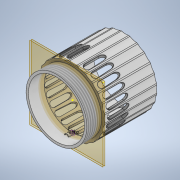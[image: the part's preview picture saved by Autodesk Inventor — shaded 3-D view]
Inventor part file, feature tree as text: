
AUTODESK INVENTOR PART (.ipt)
format: ipt  version: 2020.2 (Build 242310000, 310)  size: 3,711,488 bytes
history: native  units: mm
features: sketch x20, extrude x16, plane x16, thread x4, chamfer x3, mirror x3, pattern_circular x2, emboss x1, revolve x1, split x1, projected_geometry x1
ambient origin geometry x8: Origin, YZ Plane, XZ Plane, XY Plane, X Axis, Y Axis, Z Axis, Center Point
bodies: Solid1 (feature_tree), Solid2 (feature_tree), Solid3 (feature_tree)
feature tree (68):
  extrude  "Extrusion1"  Depth=2.0mm
  plane  "Work Plane1"
  sketch  "Sketch2"  dims[d2=4.714404mm d3=0.428883mm d4=250.0mm d6=360.0deg d8=45.0mm d9=0.0mm d11=10.0mm d12=0.0mm]
  extrude  "Extrusion2"  Depth=10.0mm
  chamfer  "Chamfer1"  Distance=250.0mm Angle=360.0deg
  chamfer  "Chamfer2"  Distance=45.0mm
  chamfer  "Chamfer3"  Distance=10.0mm
  extrude  "Extrusion3"  Depth=10.0mm TaperAngle=360.0deg
  pattern_circular  "Circular Pattern1"  Count=4 Angle=360.0deg
  sketch  "Sketch5"  dims[d18=0.9mm d19=2.0mm d20=45.0deg]
  extrude  "Extrusion4"  Depth=10.0mm TaperAngle=0.0deg
  extrude  "Extrusion5"  Depth=9.1mm TaperAngle=0.0deg
  plane  "Work Plane3"
  plane  "Work Plane4"
  extrude  "Extrusion6"  Depth=2.5mm
  plane  "Work Plane7"
  plane  "Work Plane8"
  sketch  "Sketch7"  dims[d24=0.2mm d25=2.0mm d26=45.0deg]
  plane  "Work Plane9"
  emboss  "Emboss1"
  sketch  "Sketch10"  dims[d29=20.022194mm]
  revolve  "Revolution1"  [1 undecoded]
  pattern_circular  "Circular Pattern2"  Count=3  [1 undecoded]
  extrude  "Extrusion7"  Depth=0.02mm
  sketch  "Sketch13"  dims[d32=35.0mm d33=0.0mm]
  extrude  "Extrusion8"  Depth=2.5mm
  mirror  "Mirror1"
  thread  "Thread1"  [1 undecoded]
  thread  "Thread2"  [1 undecoded]
  extrude  "Extrusion9"  [1 undecoded]
  extrude  "Extrusion10"  Depth=0.5mm TaperAngle=0.0deg
  thread  "Thread3"  [1 undecoded]
  plane  "Work Plane10"
  plane  "Work Plane11"
  split  "Split1"
  extrude  "Extrusion11"  Depth=2.5mm
  thread  "Thread4"  [1 undecoded]
  plane  "Work Plane12"
  plane  "Work Plane14"
  extrude  "Extrusion12"  Depth=4.0mm TaperAngle=0.0deg
  plane  "Work Plane15"
  mirror  "Mirror2"
  sketch  "Sketch21"  dims[d47=10.0mm d48=0.0mm d49=9.1mm d50=0.0mm]
  extrude  "Extrusion13"  [1 undecoded]
  plane  "Work Plane16"
  sketch  "Sketch22"  dims[d51=9.1mm d52=0.0mm d53=9.1mm d54=0.0mm]
  plane  "Work Plane17"
  extrude  "Extrusion14"  Depth=2.5mm TaperAngle=0.0deg
  extrude  "Extrusion15"  Depth=2.5mm TaperAngle=0.0deg
  extrude  "Extrusion16"  Depth=2.5mm TaperAngle=0.0deg
  mirror  "Mirror3"
  sketch  "Sketch1"  dims[d0=45.0mm d1=2.0mm]
  sketch  "Sketch4"  dims[d13=10.0mm d14=0.0mm d15=250.0mm d16=360.0deg]
  sketch  "Sketch6"  dims[d21=0.9mm d22=2.0mm d23=45.0deg]
  plane  "Work Plane5"
  plane  "Work Plane6"
  sketch  "Sketch9"  dims[d27=10.0mm d28=0.0mm]
  sketch  "Sketch11"  dims[d30=1.170635mm]
  sketch  "Sketch12"  dims[d31=2.0mm]
  sketch  "Sketch14"  dims[d34=90.0deg]
  sketch  "Sketch15"  dims[d35=4.0mm d36=0.0mm]
  sketch  "Sketch16"  dims[d37=11.75mm]
  sketch  "Sketch17"  dims[d38=-16.0mm d39=8.7mm d40=-8.7mm]
  sketch  "Sketch18"  dims[d41=0.2mm d42=0.0mm]
  plane  "Work Plane13"
  sketch  "Sketch20"  dims[d43=90.0deg d44=40.0mm d45=360.0deg]
  projected_geometry  "Projected Loop1"
  sketch  "Sketch23"  dims[d55=1.5mm d56=0.0mm d57=1.133755mm d58=10.0mm d59=0.0mm d60=8.847mm d61=0.0mm d62=21.5mm d63=30.0mm d64=0.02mm d65=1.586041mm d66=10.0mm d67=0.0mm d68=10.0mm d69=0.0mm d70=-2.25mm d71=0.5mm d72=0.0mm d73=-20.75mm d74=0.801779mm d75=2.939856mm d76=4.0mm d77=0.0mm d78=-1.25mm d79=2.5mm d80=0.0mm d81=1.75mm d82=0.0mm d83=2.0mm d84=0.0mm]
note: 8 required parameter values undecoded (feature->parameter linkage not recoverable at this tier; creation-order binding heuristic only, values carry confidence <= 0.55)